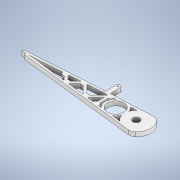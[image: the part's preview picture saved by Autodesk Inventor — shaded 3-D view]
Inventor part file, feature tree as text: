
AUTODESK INVENTOR PART (.ipt)
format: ipt  version: 2022 (Build 260153000, 153)  size: 391,168 bytes
history: native  units: mm
features: extrude x1, sketch x1
ambient origin geometry x8: Origin, YZ Plane, XZ Plane, XY Plane, X Axis, Y Axis, Z Axis, Center Point
bodies: Body1 (feature_tree)
feature tree (2):
  extrude  "Extrusion6"  Depth=10.0mm
  sketch  "Sketch1"  dims[d31=34.456mm d50=368.759386mm d57=16.0mm d69=8.0mm d70=23.0mm d71=8.0mm d73=16.0mm d80=19.0mm d81=16.0mm d82=1.0mm d83=1.0mm d84=1.0mm d85=1.0mm d86=1.0mm d87=0.8mm d88=1.0mm d90=19.0mm d94=5.0mm d95=5.0mm d105=5.0mm d106=5.0mm d108=2.0mm d109=19.0mm d114=5.0mm d115=5.0mm d116=24.0mm d117=2.5mm d118=2.5mm d123=2.5mm d124=2.5mm d125=10.0mm d126=24.0mm d127=24.0mm d128=27.0mm d135=0.5mm d136=45.0deg d139=7.0mm d165=45.0deg d169=27.0mm d175=90.0deg d181=45.0deg d185=7.0mm d186=45.0deg d190=7.0mm d191=45.0deg d197=90.0deg d203=90.0deg d206=7.0mm d209=40.0mm d210=5.0mm d211=0.0mm d212=41.0mm d213=20.0mm d214=23.0mm d215=5.0mm d216=15.0mm d217=2.0mm d218=12.0mm d219=1.5mm]
